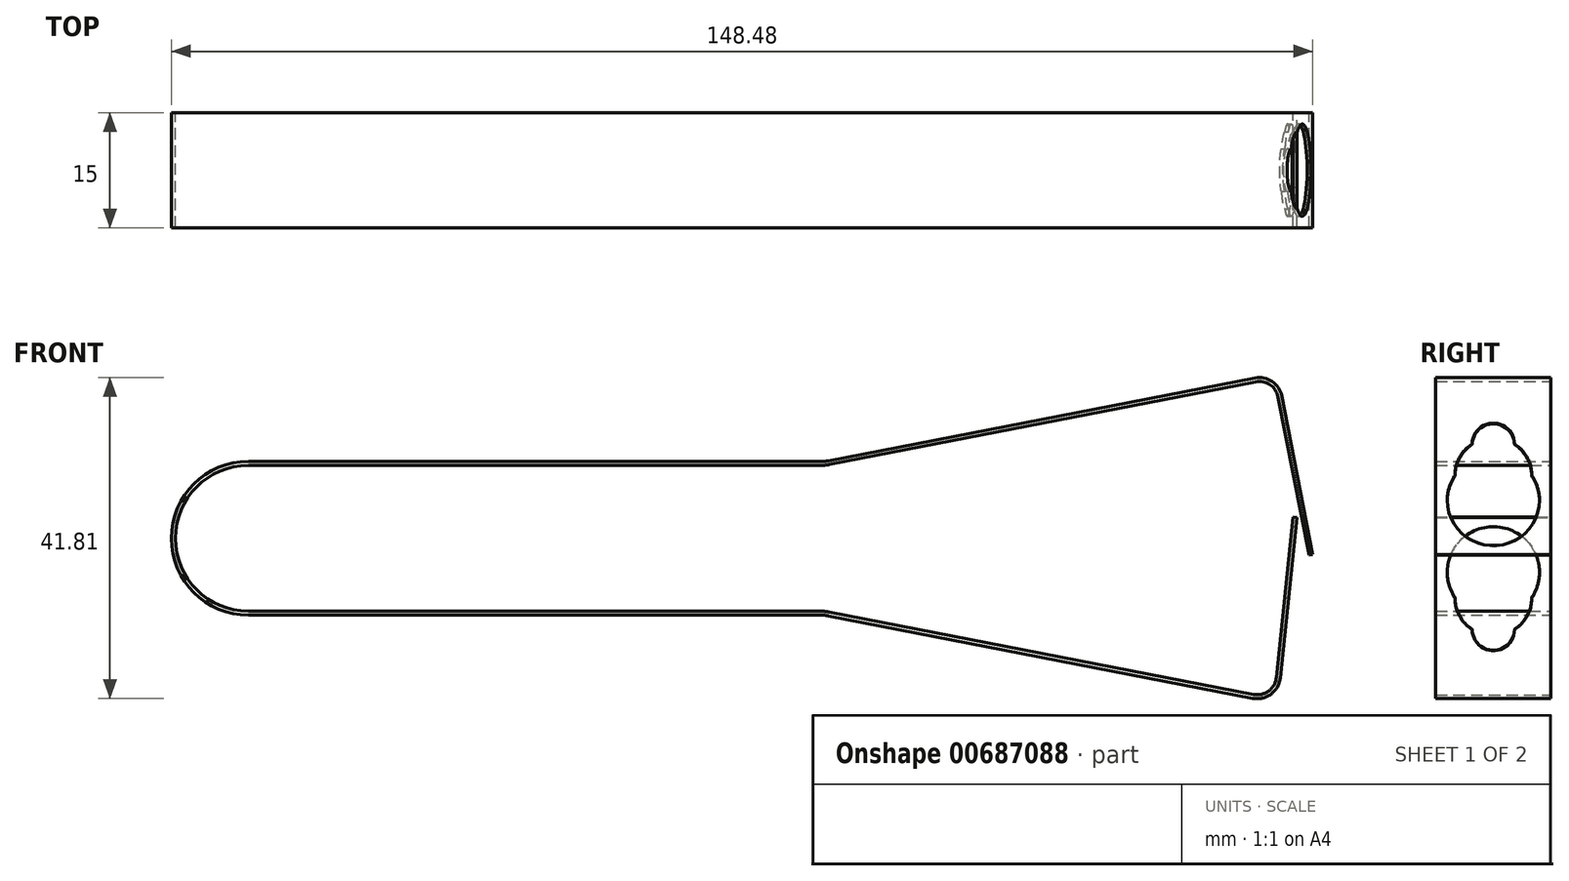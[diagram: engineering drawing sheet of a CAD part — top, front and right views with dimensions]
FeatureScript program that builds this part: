
annotation { "Feature Type Name" : "Feature", "Feature Type Description" : "" }
export const myFeature = defineFeature(function(context is Context, id is Id, definition is map)
    precondition{}
    {
        {
            var Q0;
            Q0=qCreatedBy(makeId("Front.planeOp"),FACE);
            var sketch = newSketch(context, id + "F0", { "sketchPlane" : qUnion([Q0])});
            skLineSegment(sketch, "E0", {"start": v(-75, 0) * mm, "end": v(75, 0) * mm, "construction": true});
            skArc(sketch, "E1", {"start": v(-75, 10) * mm, "mid": v(-85, 0) * mm, "end": v(-75, -10) * mm});
            skLineSegment(sketch, "E2", {"start": v(-75, 10) * mm, "end": v(-0.48, 10) * mm});
            skLineSegment(sketch, "E3", {"start": v(-75, -10) * mm, "end": v(-0.48, -10) * mm});
            skLineSegment(sketch, "E4", {"start": v(0, 10) * mm, "end": v(30, 10) * mm, "construction": true});
            skLineSegment(sketch, "E5", {"start": v(0, -10) * mm, "end": v(30, -10) * mm, "construction": true});
            skLineSegment(sketch, "E6", {"start": v(0.47, 10.1) * mm, "end": v(55.95, 20.88) * mm});
            skLineSegment(sketch, "E7", {"start": v(0.47, -10.1) * mm, "end": v(55.68, -20.82) * mm});
            skLineSegment(sketch, "E8", {"start": v(59.47, 18.5) * mm, "end": v(63.48, -2.11) * mm});
            skLineSegment(sketch, "E9", {"start": v(59.24, -18.2) * mm, "end": v(61.43, 2.7) * mm});
            skPoint(sketch, "E10.visualSharp", {"position": v(58.9, 21.45) * mm});
            skArc(sketch, "E10.filletArc", {"start": v(59.47, 18.5) * mm, "mid": v(58.2, 20.42) * mm, "end": v(55.95, 20.88) * mm});
            skPoint(sketch, "E11.visualSharp", {"position": v(58.9, -21.45) * mm});
            skArc(sketch, "E11.filletArc", {"start": v(55.68, -20.82) * mm, "mid": v(58.04, -20.3) * mm, "end": v(59.24, -18.2) * mm});
            skPoint(sketch, "E12.visualSharp", {"position": v(0, 10) * mm});
            skArc(sketch, "E12.filletArc", {"start": v(-0.48, 10) * mm, "mid": v(0, 10.02) * mm, "end": v(0.47, 10.1) * mm});
            skPoint(sketch, "E13.visualSharp", {"position": v(0, -10) * mm});
            skArc(sketch, "E13.filletArc", {"start": v(0.47, -10.1) * mm, "mid": v(0, -10.02) * mm, "end": v(-0.48, -10) * mm});
            skLineSegment(sketch, "E14.0", {"start": v(58.98, 18.4) * mm, "end": v(62.99, -2.2) * mm});
            skLineSegment(sketch, "E14.1", {"start": v(0.57, 9.6) * mm, "end": v(56.05, 20.39) * mm});
            skArc(sketch, "E14.2", {"start": v(-0.48, 9.5) * mm, "mid": v(0.05, 9.53) * mm, "end": v(0.57, 9.6) * mm});
            skLineSegment(sketch, "E14.3", {"start": v(-75, 9.5) * mm, "end": v(-0.48, 9.5) * mm});
            skArc(sketch, "E14.4", {"start": v(-75, 9.5) * mm, "mid": v(-84.5, 0) * mm, "end": v(-75, -9.5) * mm});
            skLineSegment(sketch, "E14.5", {"start": v(58.74, -18.14) * mm, "end": v(60.94, 2.74) * mm});
            skLineSegment(sketch, "E14.6", {"start": v(0.57, -9.6) * mm, "end": v(55.78, -20.33) * mm});
            skArc(sketch, "E14.7", {"start": v(0.57, -9.6) * mm, "mid": v(0.05, -9.53) * mm, "end": v(-0.48, -9.5) * mm});
            skLineSegment(sketch, "E14.8", {"start": v(-75, -9.5) * mm, "end": v(-0.48, -9.5) * mm});
            skPoint(sketch, "E15.visualSharp", {"position": v(58.46, -20.85) * mm});
            skArc(sketch, "E15.filletArc", {"start": v(55.78, -20.33) * mm, "mid": v(57.74, -19.89) * mm, "end": v(58.74, -18.14) * mm});
            skPoint(sketch, "E16.visualSharp", {"position": v(58.5, 20.86) * mm});
            skArc(sketch, "E16.filletArc", {"start": v(58.98, 18.4) * mm, "mid": v(57.92, 20) * mm, "end": v(56.05, 20.39) * mm});
            skLineSegment(sketch, "E17", {"start": v(60.94, 2.74) * mm, "end": v(61.43, 2.7) * mm});
            skLineSegment(sketch, "E18", {"start": v(62.99, -2.2) * mm, "end": v(63.48, -2.11) * mm});
            skSolve(sketch);
        }
        {
            var Q0;
            Q0 = qSketchRegion(id + "F0", true);
            extrude(context, id + "F1", {"entities" : qUnion([Q0]), "depth" : 15 * mm, "offsetDistance" : 25 * mm});
        }
        {
            var Q0;
            Q0=makeQuery(id+"F1.opExtrude","SWEPT_FACE",FACE,{"disambiguationData":[OSD([sQuery(id+"F0.wireOp",EDGE,"E8")])]});
            var sketch = newSketch(context, id + "F2", { "sketchPlane" : qUnion([Q0])});
            skLineSegment(sketch, "E19", {"start": v(-7.5, 6.82) * mm, "end": v(-7.5, -14.18) * mm, "construction": true});
            skArc(sketch, "E20", {"start": v(-10.25, 0.5) * mm, "mid": v(-11.9, -1.31) * mm, "end": v(-12.5, -3.68) * mm});
            skArc(sketch, "E21", {"start": v(-4.75, 0.5) * mm, "mid": v(-7.5, 3.24) * mm, "end": v(-10.25, 0.5) * mm});
            skArc(sketch, "E22", {"start": v(-12.5, -3.68) * mm, "mid": v(-7.5, -13) * mm, "end": v(-2.5, -3.68) * mm});
            skArc(sketch, "E23.trimOffspring", {"start": v(-2.5, -3.68) * mm, "mid": v(-3.1, -1.31) * mm, "end": v(-4.75, 0.5) * mm});
            skLineSegment(sketch, "E24", {"start": v(-8.98, 0.5) * mm, "end": v(-5.94, 0.5) * mm, "construction": true});
            skLineSegment(sketch, "E25", {"start": v(-8.9, -3.68) * mm, "end": v(-6.04, -3.68) * mm, "construction": true});
            skLineSegment(sketch, "E26", {"start": v(-9.5, -7) * mm, "end": v(-5.5, -7) * mm, "construction": true});
            skSolve(sketch);
        }
        {
            var Q0;
            Q0 = qSketchRegion(id + "F2", true);
            extrude(context, id + "F3", {"entities" : qUnion([Q0]), "operationType" : NewBodyOperationType.REMOVE, "oppositeDirection" : true, "depth" : 0.5 * mm, "offsetDistance" : 25 * mm});
        }
        {
            var Q0;
            Q0=makeQuery(id+"F1.opExtrude","SWEPT_FACE",FACE,{"disambiguationData":[OSD([sQuery(id+"F0.wireOp",EDGE,"E9")])]});
            var sketch = newSketch(context, id + "F4", { "sketchPlane" : qUnion([Q0])});
            skLineSegment(sketch, "E27", {"start": v(-7.5, 9.1) * mm, "end": v(-7.5, -11.9) * mm, "construction": true});
            skLineSegment(sketch, "E28", {"start": v(-15, -1.4) * mm, "end": v(0, -1.4) * mm, "construction": true});
            skArc(sketch, "E29", {"start": v(-12.5, -1.4) * mm, "mid": v(-11.9, -3.77) * mm, "end": v(-10.25, -5.58) * mm});
            skArc(sketch, "E30", {"start": v(-2.5, -1.4) * mm, "mid": v(-7.5, 7.92) * mm, "end": v(-12.5, -1.4) * mm});
            skLineSegment(sketch, "E31", {"start": v(-15.91, 1.92) * mm, "end": v(-1.32, 1.92) * mm, "construction": true});
            skArc(sketch, "E32", {"start": v(-10.25, -5.58) * mm, "mid": v(-7.5, -8.33) * mm, "end": v(-4.75, -5.58) * mm});
            skPoint(sketch, "E33", {"position": v(-7.5, -6.4) * mm});
            skArc(sketch, "E34.trimOffspring", {"start": v(-4.75, -5.58) * mm, "mid": v(-3.1, -3.77) * mm, "end": v(-2.5, -1.4) * mm});
            skLineSegment(sketch, "E35", {"start": v(-10.84, -5.58) * mm, "end": v(-3.32, -5.58) * mm, "construction": true});
            skSolve(sketch);
        }
        {
            var Q0;
            Q0=makeQuery(id+"F4.imprint","IMPRINT",FACE,{"disambiguationData":[TD([[makeQuery(id+"F4.imprint","IMPRINT",EDGE,{"derivedFrom":sQuery(id+"F4.wireOp",EDGE,"E29")}),1.0]])]});
            extrude(context, id + "F5", {"entities" : qUnion([Q0]), "operationType" : NewBodyOperationType.REMOVE, "oppositeDirection" : true, "depth" : 1 * mm, "offsetDistance" : 25 * mm});
        }
    });
